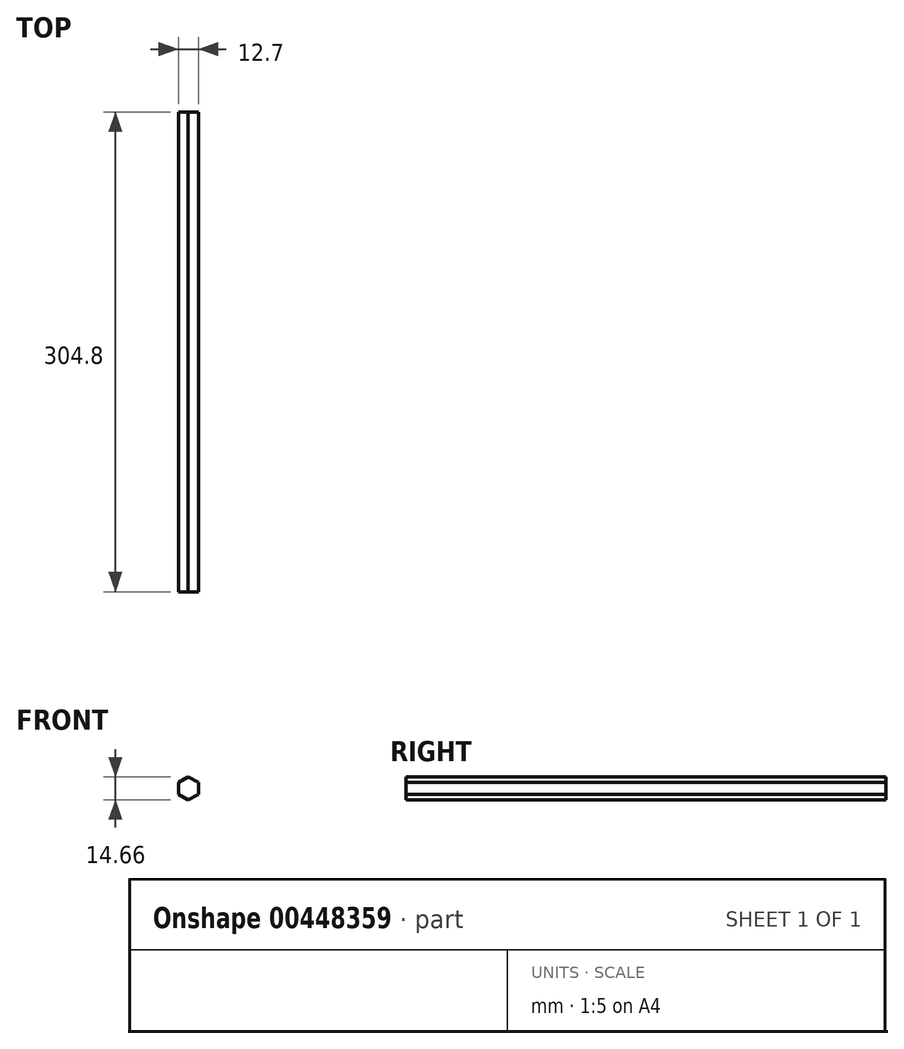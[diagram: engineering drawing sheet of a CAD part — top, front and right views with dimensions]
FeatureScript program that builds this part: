
annotation { "Feature Type Name" : "Feature", "Feature Type Description" : "" }
export const myFeature = defineFeature(function(context is Context, id is Id, definition is map)
    precondition{}
    {
        {
            var Q0;
            Q0=qCreatedBy(makeId("Front.planeOp"),FACE);
            var sketch = newSketch(context, id + "F0", { "sketchPlane" : qUnion([Q0])});
            skCircle(sketch, "E0.cCircle", {"center": v(0, 0) * mm, "radius": 6.35 * mm, "construction": true});
            skLineSegment(sketch, "E0.0", {"start": v(6.35, 3.67) * mm, "end": v(6.35, -3.67) * mm});
            skLineSegment(sketch, "E0.1", {"start": v(6.35, -3.67) * mm, "end": v(0, -7.33) * mm});
            skLineSegment(sketch, "E0.2", {"start": v(0, -7.33) * mm, "end": v(-6.35, -3.67) * mm});
            skLineSegment(sketch, "E0.3", {"start": v(-6.35, -3.67) * mm, "end": v(-6.35, 3.67) * mm});
            skLineSegment(sketch, "E0.4", {"start": v(-6.35, 3.67) * mm, "end": v(0, 7.33) * mm});
            skLineSegment(sketch, "E0.5", {"start": v(0, 7.33) * mm, "end": v(6.35, 3.67) * mm});
            skPoint(sketch, "E0.0.midPoint", {"position": v(6.35, 0) * mm});
            skSolve(sketch);
        }
        {
            var Q0;
            Q0=makeQuery(id+"F0.imprint","IMPRINT",FACE,{"disambiguationData":[TD([[makeQuery(id+"F0.imprint","IMPRINT",EDGE,{"derivedFrom":sQuery(id+"F0.wireOp",EDGE,"E0.0")}),-1.0]])]});
            extrude(context, id + "F1", {"entities" : qUnion([Q0]), "depth" : 304.8 * mm});
        }
    });
